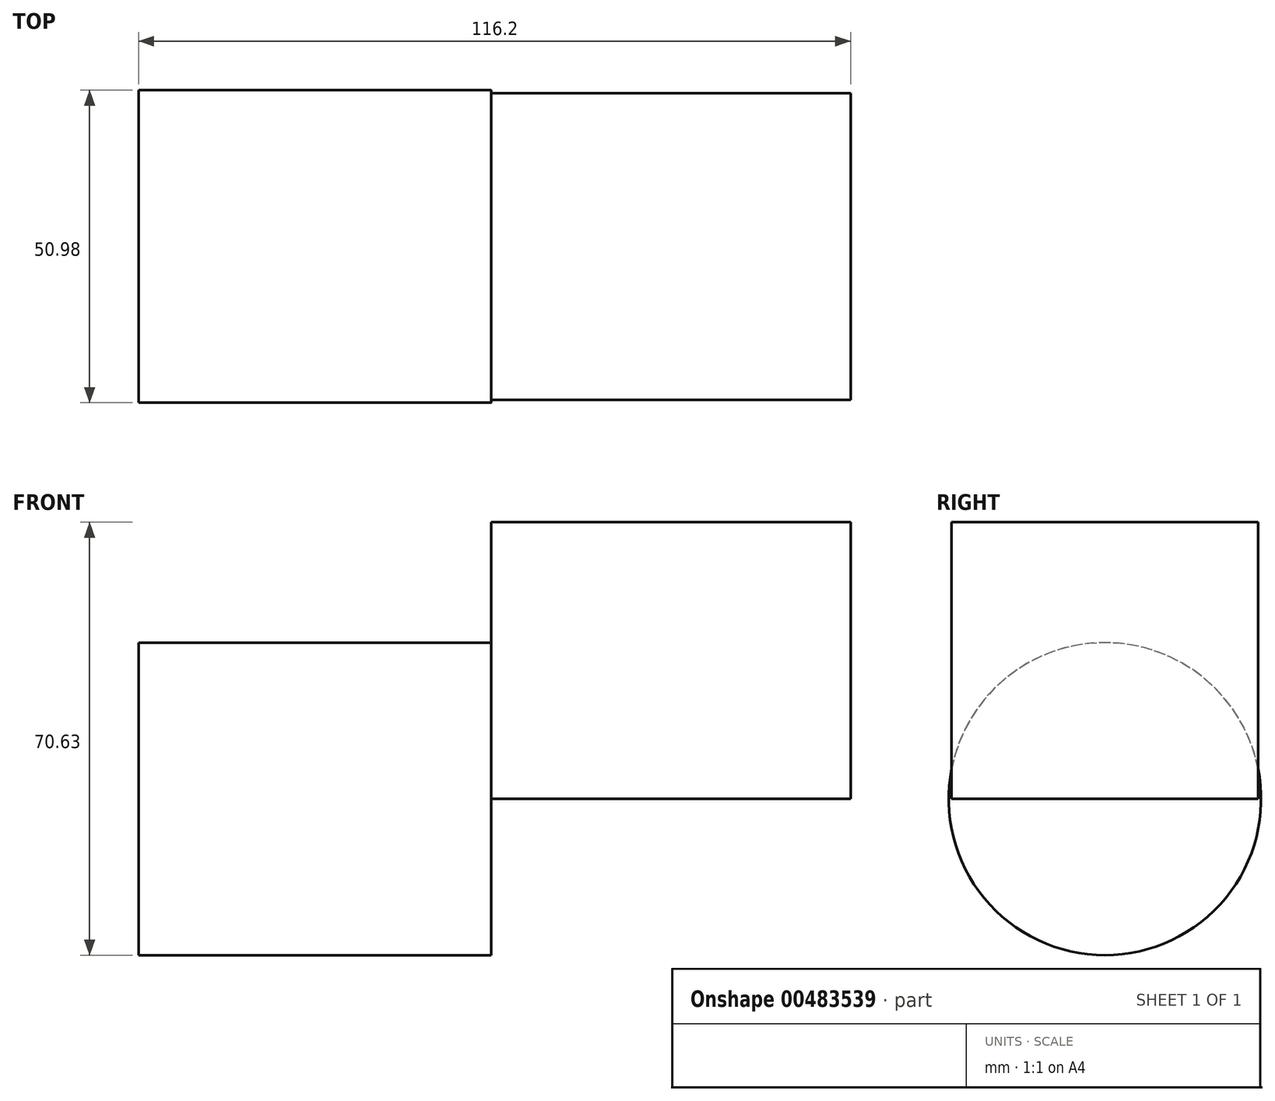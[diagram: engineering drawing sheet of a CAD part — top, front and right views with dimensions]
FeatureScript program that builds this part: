
annotation { "Feature Type Name" : "Feature", "Feature Type Description" : "" }
export const myFeature = defineFeature(function(context is Context, id is Id, definition is map)
    precondition{}
    {
        {
            var Q0;
            Q0=qCreatedBy(makeId("Front.planeOp"),FACE);
            var sketch = newSketch(context, id + "F0", { "sketchPlane" : qUnion([Q0])});
            skLineSegment(sketch, "E0.bottom", {"start": v(0, 0) * mm, "end": v(58.67, 0) * mm});
            skLineSegment(sketch, "E0.top", {"start": v(0, 45.14) * mm, "end": v(58.67, 45.14) * mm});
            skLineSegment(sketch, "E0.left", {"start": v(0, 0) * mm, "end": v(0, 45.14) * mm});
            skLineSegment(sketch, "E0.right", {"start": v(58.67, 0) * mm, "end": v(58.67, 45.14) * mm});
            skLineSegment(sketch, "E1.bottom", {"start": v(0, 0) * mm, "end": v(-57.53, 0) * mm});
            skLineSegment(sketch, "E1.top", {"start": v(0, 25.5) * mm, "end": v(-57.53, 25.5) * mm});
            skLineSegment(sketch, "E1.left", {"start": v(0, 0) * mm, "end": v(0, 25.5) * mm});
            skLineSegment(sketch, "E1.right", {"start": v(-57.53, 0) * mm, "end": v(-57.53, 25.5) * mm});
            skSolve(sketch);
        }
        {
            var Q0;
            Q0=makeQuery(id+"F0.imprint","IMPRINT",FACE,{"disambiguationData":[TD([[makeQuery(id+"F0.imprint","IMPRINT",EDGE,{"derivedFrom":sQuery(id+"F0.wireOp",EDGE,"E0.bottom")}),1.0]])]});
            extrude(context, id + "F1", {"entities" : qUnion([Q0]), "endBound" : BoundingType.SYMMETRIC, "depth" : 50 * mm, "hasSecondDirection" : true, "secondDirectionOppositeDirection" : true, "secondDirectionDepth" : 25 * mm});
        }
        {
            var Q0;
            Q0=makeQuery(id+"F0.imprint","IMPRINT",FACE,{"disambiguationData":[TD([[makeQuery(id+"F0.imprint","IMPRINT",EDGE,{"derivedFrom":sQuery(id+"F0.wireOp",EDGE,"E1.bottom")}),-1.0]])]});
            var Q1;
            Q1=sQuery(id+"F0.wireOp",EDGE,"E1.bottom");
            revolve(context, id + "F2", {"entities" : qUnion([Q0]), "axis" : qUnion([Q1]), "revolveType" : RevolveType.FULL});
        }
    });
